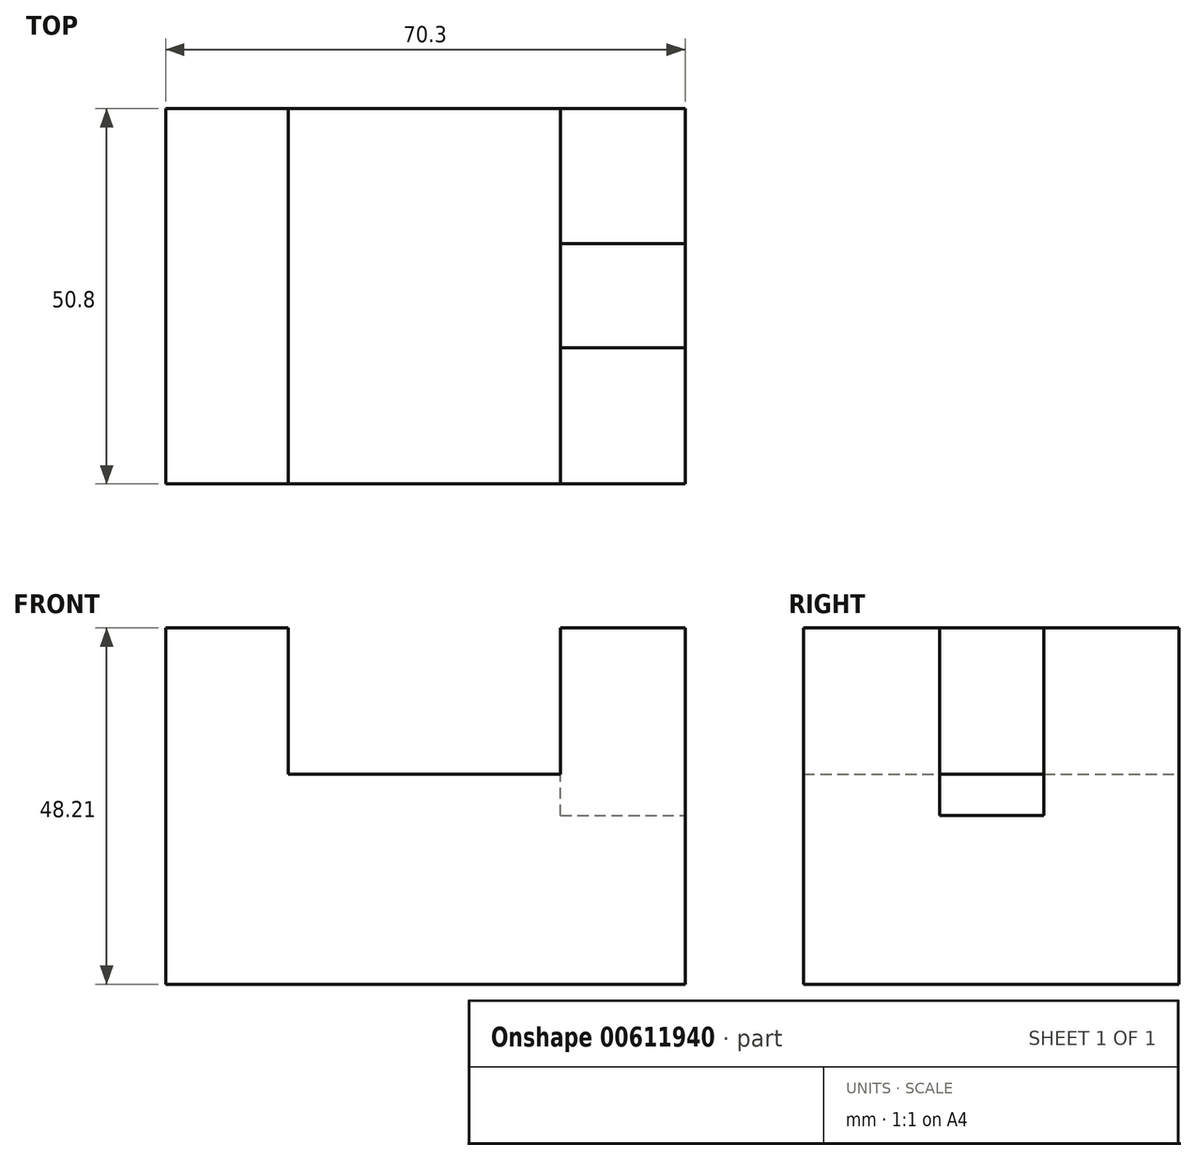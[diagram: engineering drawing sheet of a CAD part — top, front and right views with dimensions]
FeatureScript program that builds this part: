
annotation { "Feature Type Name" : "Feature", "Feature Type Description" : "" }
export const myFeature = defineFeature(function(context is Context, id is Id, definition is map)
    precondition{}
    {
        {
            var Q0;
            Q0=qCreatedBy(makeId("Front.planeOp"),FACE);
            var sketch = newSketch(context, id + "F0", { "sketchPlane" : qUnion([Q0])});
            skLineSegment(sketch, "E0.bottom", {"start": v(0, 0) * mm, "end": v(70.3, 0) * mm});
            skLineSegment(sketch, "E0.top", {"start": v(0, 48.2) * mm, "end": v(16.59, 48.2) * mm});
            skLineSegment(sketch, "E0.left", {"start": v(0, 0) * mm, "end": v(0, 48.2) * mm});
            skLineSegment(sketch, "E0.right", {"start": v(70.3, 0) * mm, "end": v(70.3, 48.2) * mm});
            skLineSegment(sketch, "E1.top", {"start": v(16.59, 28.41) * mm, "end": v(53.43, 28.41) * mm});
            skLineSegment(sketch, "E1.left", {"start": v(16.59, 48.2) * mm, "end": v(16.59, 28.41) * mm});
            skLineSegment(sketch, "E1.right", {"start": v(53.43, 48.2) * mm, "end": v(53.43, 28.41) * mm});
            skLineSegment(sketch, "E2.trimOffspring", {"start": v(53.43, 48.2) * mm, "end": v(70.3, 48.2) * mm});
            skSolve(sketch);
        }
        {
            var Q0;
            Q0=makeQuery(id+"F0.imprint","IMPRINT",FACE,{"disambiguationData":[TD([[makeQuery(id+"F0.imprint","IMPRINT",EDGE,{"derivedFrom":sQuery(id+"F0.wireOp",EDGE,"E0.bottom")}),1.0]])]});
            extrude(context, id + "F1", {"entities" : qUnion([Q0]), "endBound" : BoundingType.SYMMETRIC, "depth" : 50.8 * mm, "offsetDistance" : 25.4 * mm});
        }
        {
            var Q0;
            Q0=makeQuery(id+"F1.opExtrude","SWEPT_FACE",FACE,{"disambiguationData":[OSD([sQuery(id+"F0.wireOp",EDGE,"E2.trimOffspring")])]});
            var sketch = newSketch(context, id + "F2", { "sketchPlane" : qUnion([Q0])});
            skLineSegment(sketch, "E3.bottom", {"start": v(53.43, -6.95) * mm, "end": v(70.3, -6.95) * mm});
            skLineSegment(sketch, "E3.top", {"start": v(53.43, 7.13) * mm, "end": v(70.3, 7.13) * mm});
            skLineSegment(sketch, "E3.left", {"start": v(53.43, -6.95) * mm, "end": v(53.43, 7.13) * mm});
            skLineSegment(sketch, "E3.right", {"start": v(70.3, -6.95) * mm, "end": v(70.3, 7.13) * mm});
            skSolve(sketch);
        }
        {
            var Q0;
            Q0=makeQuery(id+"F2.imprint","IMPRINT",FACE,{"disambiguationData":[TD([[makeQuery(id+"F2.imprint","IMPRINT",EDGE,{"derivedFrom":sQuery(id+"F2.wireOp",EDGE,"E3.bottom")}),1.0]])]});
            extrude(context, id + "F3", {"entities" : qUnion([Q0]), "operationType" : NewBodyOperationType.REMOVE, "oppositeDirection" : true, "depth" : 25.4 * mm, "offsetDistance" : 25.4 * mm});
        }
    });
